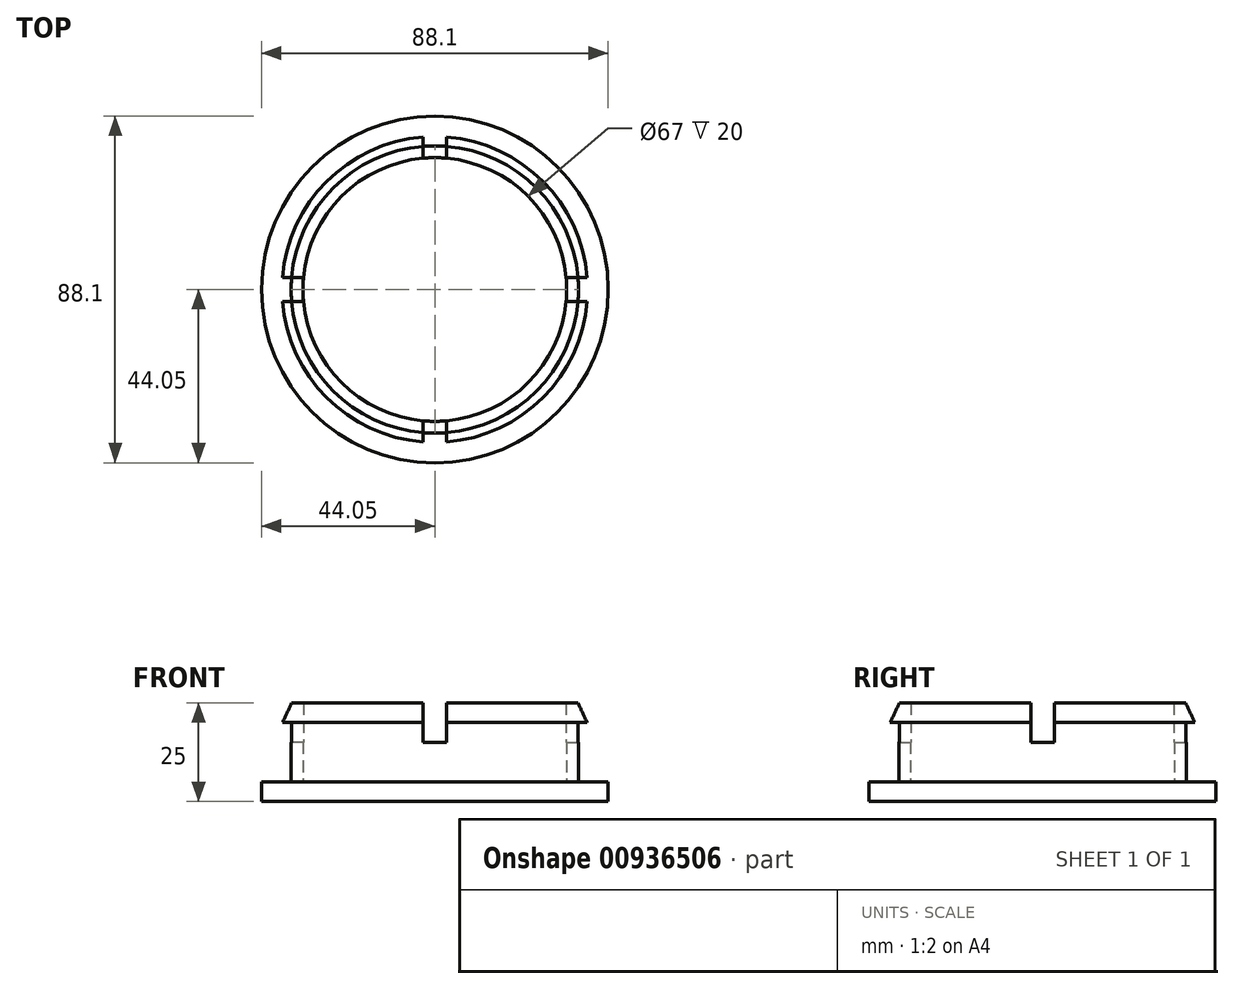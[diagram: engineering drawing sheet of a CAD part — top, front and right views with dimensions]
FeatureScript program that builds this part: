
annotation { "Feature Type Name" : "Feature", "Feature Type Description" : "" }
export const myFeature = defineFeature(function(context is Context, id is Id, definition is map)
    precondition{}
    {
        {
            var Q0;
            Q0=qCreatedBy(makeId("Top.planeOp"),FACE);
            var sketch = newSketch(context, id + "F0", { "sketchPlane" : qUnion([Q0])});
            skCircle(sketch, "E0", {"center": v(0, 0) * mm, "radius": 36.5 * mm});
            skCircle(sketch, "E1.0", {"center": v(0, 0) * mm, "radius": 33.5 * mm});
            skSolve(sketch);
        }
        {
            var Q0;
            Q0=qSketchRegion(id+"F0",true);
            extrude(context, id + "F1", {"entities" : qUnion([Q0]), "depth" : 20 * mm, "offsetDistance" : 25 * mm});
        }
        {
            var Q0;
            Q0=makeQuery(id+"F1.opExtrude","CAP_FACE",FACE,{"disambiguationData":[OSD([sQuery(id+"F0.wireOp",EDGE,"E0"),sQuery(id+"F0.wireOp",EDGE,"E1.0")])],"isStart":false});
            var sketch = newSketch(context, id + "F2", { "sketchPlane" : qUnion([Q0])});
            skCircle(sketch, "E2.0", {"center": v(0, 0) * mm, "radius": 36.5 * mm});
            skSolve(sketch);
        }
        {
            var Q0;
            Q0=qSketchRegion(id+"F2",true);
            extrude(context, id + "F3", {"entities" : qUnion([Q0]), "operationType" : NewBodyOperationType.ADD, "oppositeDirection" : true, "depth" : 5 * mm, "offsetDistance" : 25 * mm, "hasDraft" : true, "draftAngle" : 25 * degree});
        }
        {
            var Q0;
            Q0=makeQuery(id+"F3.boolean.opBoolean","SPLIT",FACE,{"disambiguationData":[TD([makeQuery(id+"F1.opExtrude","SWEPT_FACE",FACE,{"disambiguationData":[OSD([sQuery(id+"F0.wireOp",EDGE,"E1.0")])]})])],"derivedFrom":makeQuery(id+"F3.opExtrude","CAP_FACE",FACE,{"disambiguationData":[OSD([sQuery(id+"F2.wireOp",EDGE,"E2.0")])],"isStart":false})});
            var sketch = newSketch(context, id + "F4", { "sketchPlane" : qUnion([Q0])});
            skSolve(sketch);
        }
        {
            var Q0;
            Q0=qSketchRegion(id+"F4",true);
            var Q1;
            Q1=makeQuery(id+"F4.imprint","IMPRINT",FACE,{"disambiguationData":[TD([[makeQuery(id+"F4.imprint","IMPRINT",EDGE,{"derivedFrom":makeQuery(id+"F3.boolean.opBoolean","INTERSECT",EDGE,{"derivedFrom":[makeQuery(id+"F1.opExtrude","SWEPT_FACE",FACE,{"disambiguationData":[OSD([sQuery(id+"F0.wireOp",EDGE,"E1.0")])]}),makeQuery(id+"F3.opExtrude","CAP_FACE",FACE,{"disambiguationData":[OSD([sQuery(id+"F2.wireOp",EDGE,"E2.0")])],"isStart":false})]})}),-1.0]])]});
            extrude(context, id + "F5", {"entities" : qUnion([Q0, Q1]), "operationType" : NewBodyOperationType.REMOVE, "oppositeDirection" : true, "depth" : 25 * mm, "offsetDistance" : 25 * mm});
        }
        {
            var Q0;
            Q0=makeQuery(id+"F1.opExtrude","CAP_FACE",FACE,{"disambiguationData":[OSD([sQuery(id+"F0.wireOp",EDGE,"E0"),sQuery(id+"F0.wireOp",EDGE,"E1.0")])],"isStart":true});
            var sketch = newSketch(context, id + "F6", { "sketchPlane" : qUnion([Q0])});
            skCircle(sketch, "E3.0", {"center": v(0, 0) * mm, "radius": 44.05 * mm});
            skSolve(sketch);
        }
        {
            var Q0;
            Q0=qSketchRegion(id+"F6",true);
            extrude(context, id + "F7", {"entities" : qUnion([Q0]), "operationType" : NewBodyOperationType.ADD, "depth" : 5 * mm, "offsetDistance" : 25 * mm});
        }
        {
            var Q0;
            Q0=makeQuery(id+"F7.boolean.opBoolean","SPLIT",FACE,{"disambiguationData":[TD([makeQuery(id+"F1.opExtrude","SWEPT_FACE",FACE,{"disambiguationData":[OSD([sQuery(id+"F0.wireOp",EDGE,"E1.0")])]})])],"derivedFrom":makeQuery(id+"F7.opExtrude","CAP_FACE",FACE,{"disambiguationData":[OSD([sQuery(id+"F6.wireOp",EDGE,"E3.0")])],"isStart":true})});
            var Q1;
            Q1=makeQuery(id+"F3.boolean.opBoolean","MERGE",FACE,{"derivedFrom":[makeQuery(id+"F1.opExtrude","CAP_FACE",FACE,{"disambiguationData":[OSD([sQuery(id+"F0.wireOp",EDGE,"E0"),sQuery(id+"F0.wireOp",EDGE,"E1.0")])],"isStart":false}),makeQuery(id+"F3.opExtrude","CAP_FACE",FACE,{"disambiguationData":[OSD([sQuery(id+"F2.wireOp",EDGE,"E2.0")])],"isStart":true})]});
            cPlane(context, id + "F8", {"entities" : qUnion([Q0, Q1]), "cplaneType" : CPlaneType.MID_PLANE, "offset" : 25 * mm, "width" : 150 * mm, "height" : 150 * mm});
        }
        {
            var Q0;
            Q0=qCreatedBy(id+"F8.planeOp",FACE);
            var sketch = newSketch(context, id + "F9", { "sketchPlane" : qUnion([Q0])});
            skLineSegment(sketch, "E4.1", {"start": v(3, 3) * mm, "end": v(35.05, 3) * mm});
            skArc(sketch, "E5.0", {"start": v(3, 38.38) * mm, "mid": v(0, 38.5) * mm, "end": v(-3, 38.38) * mm});
            skLineSegment(sketch, "E6.MirrorCS", {"start": v(-3, -3) * mm, "end": v(-3, -40.27) * mm});
            skLineSegment(sketch, "E7.MirrorCS", {"start": v(-3, 3) * mm, "end": v(-38.38, 3) * mm});
            skLineSegment(sketch, "E8.MirrorCS", {"start": v(-38.39, 0) * mm, "end": v(-38.5, 0) * mm});
            skLineSegment(sketch, "E9.MirrorCS", {"start": v(-3, 3) * mm, "end": v(-3, 35.05) * mm});
            skLineSegment(sketch, "E10.MirrorCS", {"start": v(-3, 3) * mm, "end": v(-38.4, 2.88) * mm});
            skLineSegment(sketch, "E11.MirrorCS", {"start": v(3, 3) * mm, "end": v(61.4, 3) * mm});
            skLineSegment(sketch, "E12.MirrorCS", {"start": v(3, 3) * mm, "end": v(3, 35.05) * mm});
            skPoint(sketch, "E13.orphan", {"position": v(-33.5, 0) * mm});
            skPoint(sketch, "E14.orphan", {"position": v(-35.05, 3) * mm});
            skPoint(sketch, "E15.orphan", {"position": v(-33.5, 2.9) * mm});
            skPoint(sketch, "E16.orphan", {"position": v(-3, -35.05) * mm});
            skPoint(sketch, "E17.orphan", {"position": v(1.55, 0) * mm});
            skPoint(sketch, "E18.end.orphan", {"position": v(35.05, 0) * mm});
            skLineSegment(sketch, "E19.bottom", {"start": v(-38.38, 3) * mm, "end": v(-3, 3) * mm});
            skLineSegment(sketch, "E19.top", {"start": v(-38.38, 3) * mm, "end": v(-3, 3) * mm});
            skLineSegment(sketch, "E19.right", {"start": v(38.38, 3) * mm, "end": v(38.38, 3) * mm});
            skPoint(sketch, "E19.middle", {"position": v(0, 3) * mm});
            skLineSegment(sketch, "E20.left", {"start": v(-3, -40.27) * mm, "end": v(-3, -3) * mm});
            skLineSegment(sketch, "E20.right", {"start": v(3, -40.27) * mm, "end": v(3, -3) * mm});
            skLineSegment(sketch, "E21.bottom", {"start": v(-61.4, 3) * mm, "end": v(-3, 3) * mm});
            skLineSegment(sketch, "E21.top", {"start": v(-61.4, 3) * mm, "end": v(-3, 3) * mm});
            skLineSegment(sketch, "E21.left", {"start": v(-61.4, 3) * mm, "end": v(-61.4, 3) * mm});
            skLineSegment(sketch, "E21.right", {"start": v(61.4, 3) * mm, "end": v(61.4, 3) * mm});
            skLineSegment(sketch, "E22.bottom", {"start": v(3, -53.78) * mm, "end": v(-3, -53.78) * mm});
            skLineSegment(sketch, "E22.top", {"start": v(3, 53.78) * mm, "end": v(-3, 53.78) * mm});
            skLineSegment(sketch, "E22.left", {"start": v(3, -53.78) * mm, "end": v(3, -3) * mm});
            skLineSegment(sketch, "E22.right", {"start": v(-3, -53.78) * mm, "end": v(-3, -3) * mm});
            skPoint(sketch, "E22.cornerSnap0", {"position": v(3, 0) * mm});
            skLineSegment(sketch, "E23.trimOffspring", {"start": v(-3, 3) * mm, "end": v(-3, 53.78) * mm});
            skLineSegment(sketch, "E24.trimOffspring", {"start": v(-3, 3) * mm, "end": v(-3, 40.27) * mm});
            skLineSegment(sketch, "E25.trimOffspring", {"start": v(3, 3) * mm, "end": v(38.38, 3) * mm});
            skLineSegment(sketch, "E26.trimOffspring", {"start": v(3, 3) * mm, "end": v(3, 53.78) * mm});
            skLineSegment(sketch, "E27.trimOffspring", {"start": v(3, 3) * mm, "end": v(3, 40.27) * mm});
            skLineSegment(sketch, "E28.bottom", {"start": v(61.4, 3) * mm, "end": v(3, 3) * mm});
            skLineSegment(sketch, "E28.top", {"start": v(61.4, -3) * mm, "end": v(3, -3) * mm});
            skLineSegment(sketch, "E28.left", {"start": v(61.4, 3) * mm, "end": v(61.4, -3) * mm});
            skLineSegment(sketch, "E28.right", {"start": v(-61.4, 3) * mm, "end": v(-61.4, -3) * mm});
            skLineSegment(sketch, "E29.trimOffspring", {"start": v(3, -3) * mm, "end": v(3, -29.05) * mm});
            skLineSegment(sketch, "E30.trimOffspring", {"start": v(-3, 3) * mm, "end": v(-61.4, 3) * mm});
            skLineSegment(sketch, "E31.trimOffspring", {"start": v(-3, -3) * mm, "end": v(-61.4, -3) * mm});
            skSolve(sketch);
        }
        {
            var Q0;
            Q0=qSketchRegion(id+"F9",true);
            extrude(context, id + "F10", {"entities" : qUnion([Q0]), "operationType" : NewBodyOperationType.REMOVE, "depth" : 25 * mm, "offsetDistance" : 25 * mm});
        }
    });
